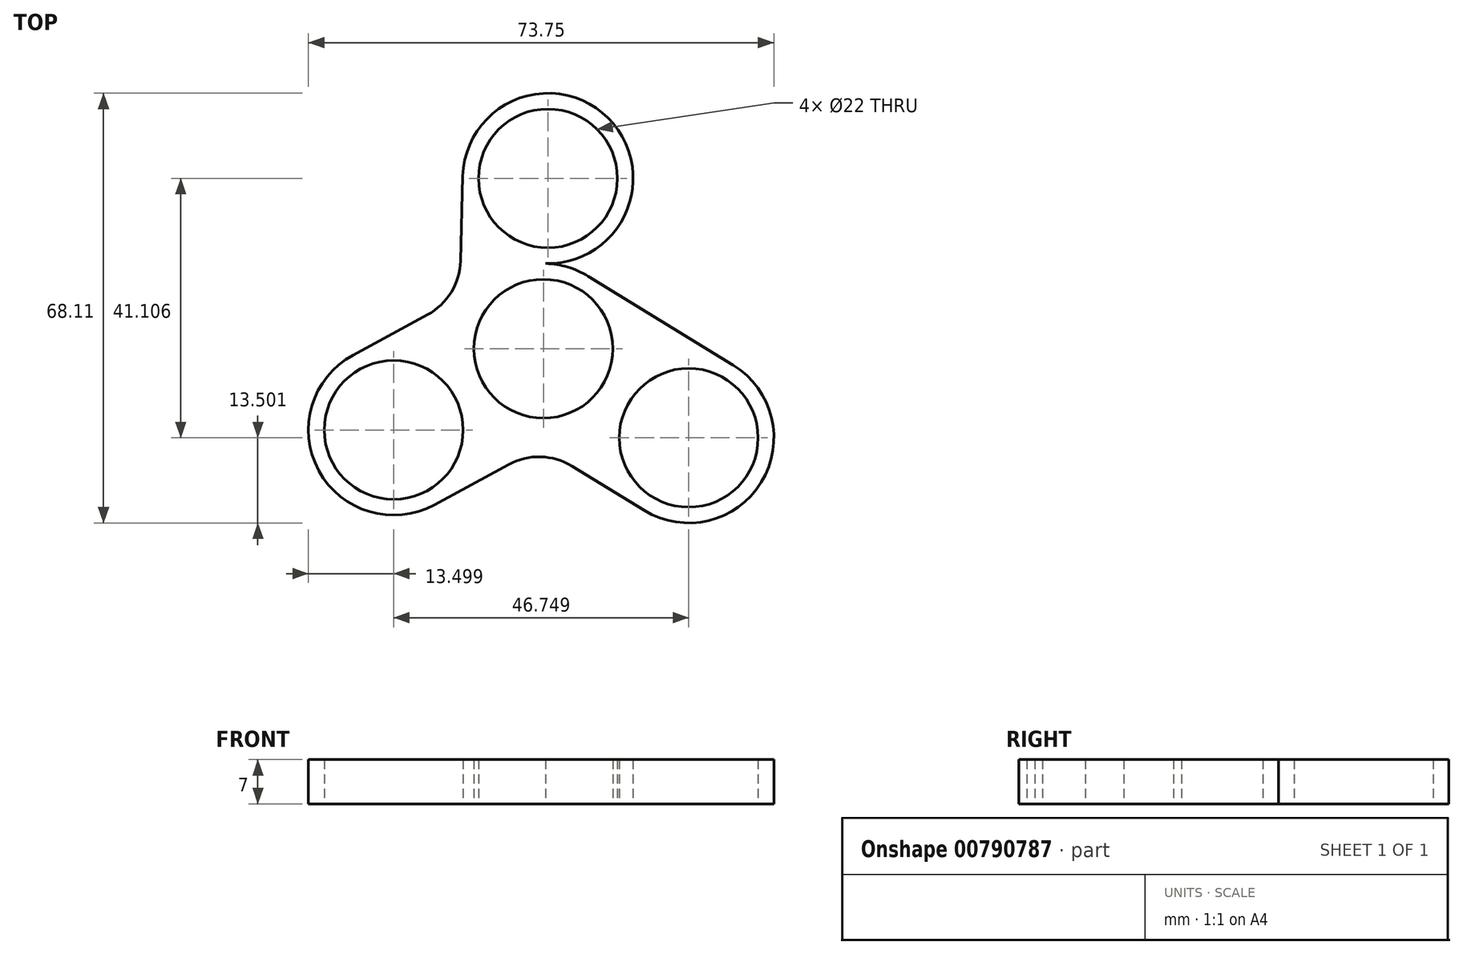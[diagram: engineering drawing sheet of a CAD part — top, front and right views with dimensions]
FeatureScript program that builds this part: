
annotation { "Feature Type Name" : "Feature", "Feature Type Description" : "" }
export const myFeature = defineFeature(function(context is Context, id is Id, definition is map)
    precondition{}
    {
        {
            var Q0;
            Q0=qCreatedBy(makeId("Top.planeOp"),FACE);
            var sketch = newSketch(context, id + "F0", { "sketchPlane" : qUnion([Q0])});
            skCircle(sketch, "E0", {"center": v(-20.47, -6.66) * mm, "radius": 13.5 * mm});
            skCircle(sketch, "E1", {"center": v(3.98, 33.2) * mm, "radius": 13.5 * mm});
            skCircle(sketch, "E2", {"center": v(26.28, -7.9) * mm, "radius": 13.5 * mm});
            skLineSegment(sketch, "E3", {"start": v(3.98, 33.2) * mm, "end": v(-20.47, -6.66) * mm, "construction": true});
            skLineSegment(sketch, "E4", {"start": v(3.98, 33.2) * mm, "end": v(26.28, -7.9) * mm, "construction": true});
            skCircle(sketch, "E5", {"center": v(3.26, 6.22) * mm, "radius": 13.5 * mm});
            skLineSegment(sketch, "E6", {"start": v(-20.47, -6.66) * mm, "end": v(26.28, -7.9) * mm, "construction": true});
            skLineSegment(sketch, "E7", {"start": v(-20.47, -6.66) * mm, "end": v(3.26, 6.22) * mm, "construction": true});
            skLineSegment(sketch, "E8", {"start": v(3.98, 33.2) * mm, "end": v(3.26, 6.22) * mm, "construction": true});
            skLineSegment(sketch, "E9", {"start": v(3.26, 6.22) * mm, "end": v(26.28, -7.9) * mm, "construction": true});
            skLineSegment(sketch, "E10", {"start": v(-26.9, 5.2) * mm, "end": v(-3.18, 18.08) * mm});
            skLineSegment(sketch, "E11", {"start": v(-9.52, 33.56) * mm, "end": v(-10.23, 6.57) * mm});
            skLineSegment(sketch, "E12", {"start": v(17.45, 33.97) * mm, "end": v(16.76, 5.88) * mm});
            skLineSegment(sketch, "E13", {"start": v(19.22, -19.4) * mm, "end": v(-3.8, -5.3) * mm});
            skLineSegment(sketch, "E14", {"start": v(10.32, 17.72) * mm, "end": v(33.34, 3.6) * mm});
            skLineSegment(sketch, "E15", {"start": v(-14.03, -18.53) * mm, "end": v(9.7, -5.65) * mm});
            skCircle(sketch, "E16", {"center": v(3.98, 33.2) * mm, "radius": 11 * mm});
            skCircle(sketch, "E17", {"center": v(26.28, -7.9) * mm, "radius": 11 * mm});
            skCircle(sketch, "E18", {"center": v(-20.47, -6.66) * mm, "radius": 11 * mm});
            skCircle(sketch, "E19", {"center": v(3.26, 6.22) * mm, "radius": 11 * mm});
            skSolve(sketch);
        }
        {
            var Q0;
            {var subQ0=sQuery(id+"F0.wireOp",EDGE,"E5");var subQ5=makeQuery(id+"F0.imprint","INTERSECT",VERTEX,{"derivedFrom":[subQ0,sQuery(id+"F0.wireOp",EDGE,"E14")]});Q0=makeQuery(id+"F0.imprint","IMPRINT",FACE,{"disambiguationData":[TD([[makeQuery(id+"F0.imprint","IMPRINT",EDGE,{"disambiguationData":[TD([[subQ5,-1.0]])],"derivedFrom":subQ0}),1.0]])]});}
            var Q1;
            {var subQ0=sQuery(id+"F0.wireOp",EDGE,"E0");var subQ1=makeQuery(id+"F0.imprint","INTERSECT",VERTEX,{"derivedFrom":[subQ0,sQuery(id+"F0.wireOp",EDGE,"E10")]});Q1=makeQuery(id+"F0.imprint","IMPRINT",FACE,{"disambiguationData":[TD([[makeQuery(id+"F0.imprint","IMPRINT",EDGE,{"disambiguationData":[TD([[subQ1,1.0]])],"derivedFrom":subQ0}),1.0]])]});}
            var Q2;
            {var subQ0=sQuery(id+"F0.wireOp",EDGE,"E2");var subQ1=makeQuery(id+"F0.imprint","INTERSECT",VERTEX,{"derivedFrom":[subQ0,sQuery(id+"F0.wireOp",EDGE,"E14")]});Q2=makeQuery(id+"F0.imprint","IMPRINT",FACE,{"disambiguationData":[TD([[makeQuery(id+"F0.imprint","IMPRINT",EDGE,{"disambiguationData":[TD([[subQ1,-1.0]])],"derivedFrom":subQ0}),1.0]])]});}
            var Q3;
            {var subQ0=sQuery(id+"F0.wireOp",EDGE,"E10");var subQ1=sQuery(id+"F0.wireOp",EDGE,"E0");var subQ2=makeQuery(id+"F0.imprint","INTERSECT",VERTEX,{"derivedFrom":[subQ1,subQ0]});Q3=makeQuery(id+"F0.imprint","IMPRINT",FACE,{"disambiguationData":[TD([[makeQuery(id+"F0.imprint","IMPRINT",EDGE,{"disambiguationData":[TD([[subQ2,1.0]])],"derivedFrom":subQ1}),-1.0]])]});}
            var Q4;
            {var subQ0=sQuery(id+"F0.wireOp",EDGE,"E15");var subQ1=sQuery(id+"F0.wireOp",EDGE,"E0");var subQ2=makeQuery(id+"F0.imprint","INTERSECT",VERTEX,{"derivedFrom":[subQ1,subQ0]});Q4=makeQuery(id+"F0.imprint","IMPRINT",FACE,{"disambiguationData":[TD([[makeQuery(id+"F0.imprint","IMPRINT",EDGE,{"disambiguationData":[TD([[subQ2,-1.0]])],"derivedFrom":subQ1}),-1.0]])]});}
            var Q5;
            {var subQ0=sQuery(id+"F0.wireOp",EDGE,"E1");var subQ1=makeQuery(id+"F0.imprint","INTERSECT",VERTEX,{"derivedFrom":[subQ0,sQuery(id+"F0.wireOp",EDGE,"E11")]});Q5=makeQuery(id+"F0.imprint","IMPRINT",FACE,{"disambiguationData":[TD([[makeQuery(id+"F0.imprint","IMPRINT",EDGE,{"disambiguationData":[TD([[subQ1,1.0]])],"derivedFrom":subQ0}),1.0]])]});}
            var Q6;
            {var subQ0=sQuery(id+"F0.wireOp",EDGE,"E11");var subQ1=sQuery(id+"F0.wireOp",EDGE,"E1");var subQ2=makeQuery(id+"F0.imprint","INTERSECT",VERTEX,{"derivedFrom":[subQ1,subQ0]});Q6=makeQuery(id+"F0.imprint","IMPRINT",FACE,{"disambiguationData":[TD([[makeQuery(id+"F0.imprint","IMPRINT",EDGE,{"disambiguationData":[TD([[subQ2,-1.0]])],"derivedFrom":subQ1}),-1.0]])]});}
            var Q7;
            {var subQ0=sQuery(id+"F0.wireOp",EDGE,"E12");var subQ1=sQuery(id+"F0.wireOp",EDGE,"E1");var subQ2=makeQuery(id+"F0.imprint","INTERSECT",VERTEX,{"disambiguationData":[OD(1.0)],"derivedFrom":[subQ1,subQ0]});Q7=makeQuery(id+"F0.imprint","IMPRINT",FACE,{"disambiguationData":[TD([[makeQuery(id+"F0.imprint","IMPRINT",EDGE,{"disambiguationData":[TD([[subQ2,1.0]])],"derivedFrom":subQ1}),-1.0]])]});}
            var Q8;
            {var subQ0=sQuery(id+"F0.wireOp",EDGE,"E14");var subQ1=sQuery(id+"F0.wireOp",EDGE,"E2");var subQ2=makeQuery(id+"F0.imprint","INTERSECT",VERTEX,{"derivedFrom":[subQ1,subQ0]});Q8=makeQuery(id+"F0.imprint","IMPRINT",FACE,{"disambiguationData":[TD([[makeQuery(id+"F0.imprint","IMPRINT",EDGE,{"disambiguationData":[TD([[subQ2,-1.0]])],"derivedFrom":subQ1}),-1.0]])]});}
            var Q9;
            {var subQ0=sQuery(id+"F0.wireOp",EDGE,"E13");var subQ1=sQuery(id+"F0.wireOp",EDGE,"E2");var subQ2=makeQuery(id+"F0.imprint","INTERSECT",VERTEX,{"derivedFrom":[subQ1,subQ0]});Q9=makeQuery(id+"F0.imprint","IMPRINT",FACE,{"disambiguationData":[TD([[makeQuery(id+"F0.imprint","IMPRINT",EDGE,{"disambiguationData":[TD([[subQ2,1.0]])],"derivedFrom":subQ1}),-1.0]])]});}
            var Q10;
            {var subQ0=sQuery(id+"F0.wireOp",EDGE,"E10");var subQ1=sQuery(id+"F0.wireOp",EDGE,"E5");var subQ2=makeQuery(id+"F0.imprint","INTERSECT",VERTEX,{"derivedFrom":[subQ1,subQ0]});Q10=makeQuery(id+"F0.imprint","IMPRINT",FACE,{"disambiguationData":[TD([[makeQuery(id+"F0.imprint","IMPRINT",EDGE,{"disambiguationData":[TD([[subQ2,-1.0]])],"derivedFrom":subQ1}),-1.0]])]});}
            var Q11;
            {var subQ0=sQuery(id+"F0.wireOp",EDGE,"E13");var subQ1=sQuery(id+"F0.wireOp",EDGE,"E5");var subQ2=makeQuery(id+"F0.imprint","INTERSECT",VERTEX,{"derivedFrom":[subQ1,subQ0]});Q11=makeQuery(id+"F0.imprint","IMPRINT",FACE,{"disambiguationData":[TD([[makeQuery(id+"F0.imprint","IMPRINT",EDGE,{"disambiguationData":[TD([[subQ2,-1.0]])],"derivedFrom":subQ1}),-1.0]])]});}
            var Q12;
            {var subQ0=sQuery(id+"F0.wireOp",EDGE,"E12");var subQ1=sQuery(id+"F0.wireOp",EDGE,"E5");var subQ2=makeQuery(id+"F0.imprint","INTERSECT",VERTEX,{"derivedFrom":[subQ1,subQ0]});Q12=makeQuery(id+"F0.imprint","IMPRINT",FACE,{"disambiguationData":[TD([[makeQuery(id+"F0.imprint","IMPRINT",EDGE,{"disambiguationData":[TD([[subQ2,-1.0]])],"derivedFrom":subQ1}),-1.0]])]});}
            var Q13;
            {var subQ0=sQuery(id+"F0.wireOp",EDGE,"E12");var subQ1=sQuery(id+"F0.wireOp",EDGE,"E1");var subQ2=makeQuery(id+"F0.imprint","INTERSECT",VERTEX,{"disambiguationData":[OD(0.0)],"derivedFrom":[subQ1,subQ0]});Q13=makeQuery(id+"F0.imprint","IMPRINT",FACE,{"disambiguationData":[TD([[makeQuery(id+"F0.imprint","IMPRINT",EDGE,{"disambiguationData":[TD([[subQ2,1.0]])],"derivedFrom":subQ1}),1.0]])]});}
            extrude(context, id + "F1", {"entities" : qUnion([Q0, Q1, Q2, Q3, Q4, Q5, Q6, Q7, Q8, Q9, Q10, Q11, Q12, Q13]), "depth" : 7 * mm, "offsetDistance" : 25 * mm});
        }
        {
            var Q0;
            Q0=makeQuery(id+"F1.opExtrude","SWEPT_EDGE",EDGE,{"disambiguationData":[OSD([sQuery(id+"F0.wireOp",EDGE,"E10"),sQuery(id+"F0.wireOp",EDGE,"E11")])]});
            var Q1;
            Q1=makeQuery(id+"F1.opExtrude","SWEPT_EDGE",EDGE,{"disambiguationData":[OSD([sQuery(id+"F0.wireOp",EDGE,"E12"),sQuery(id+"F0.wireOp",EDGE,"E14")])]});
            var Q2;
            Q2=makeQuery(id+"F1.opExtrude","SWEPT_EDGE",EDGE,{"disambiguationData":[OSD([sQuery(id+"F0.wireOp",EDGE,"E13"),sQuery(id+"F0.wireOp",EDGE,"E15")])]});
            fillet(context, id + "F2", {"entities" : qUnion([Q0, Q1, Q2]), "radius" : 10 * mm, "tangentPropagation" : true, "allowEdgeOverflow" : false});
        }
    });
